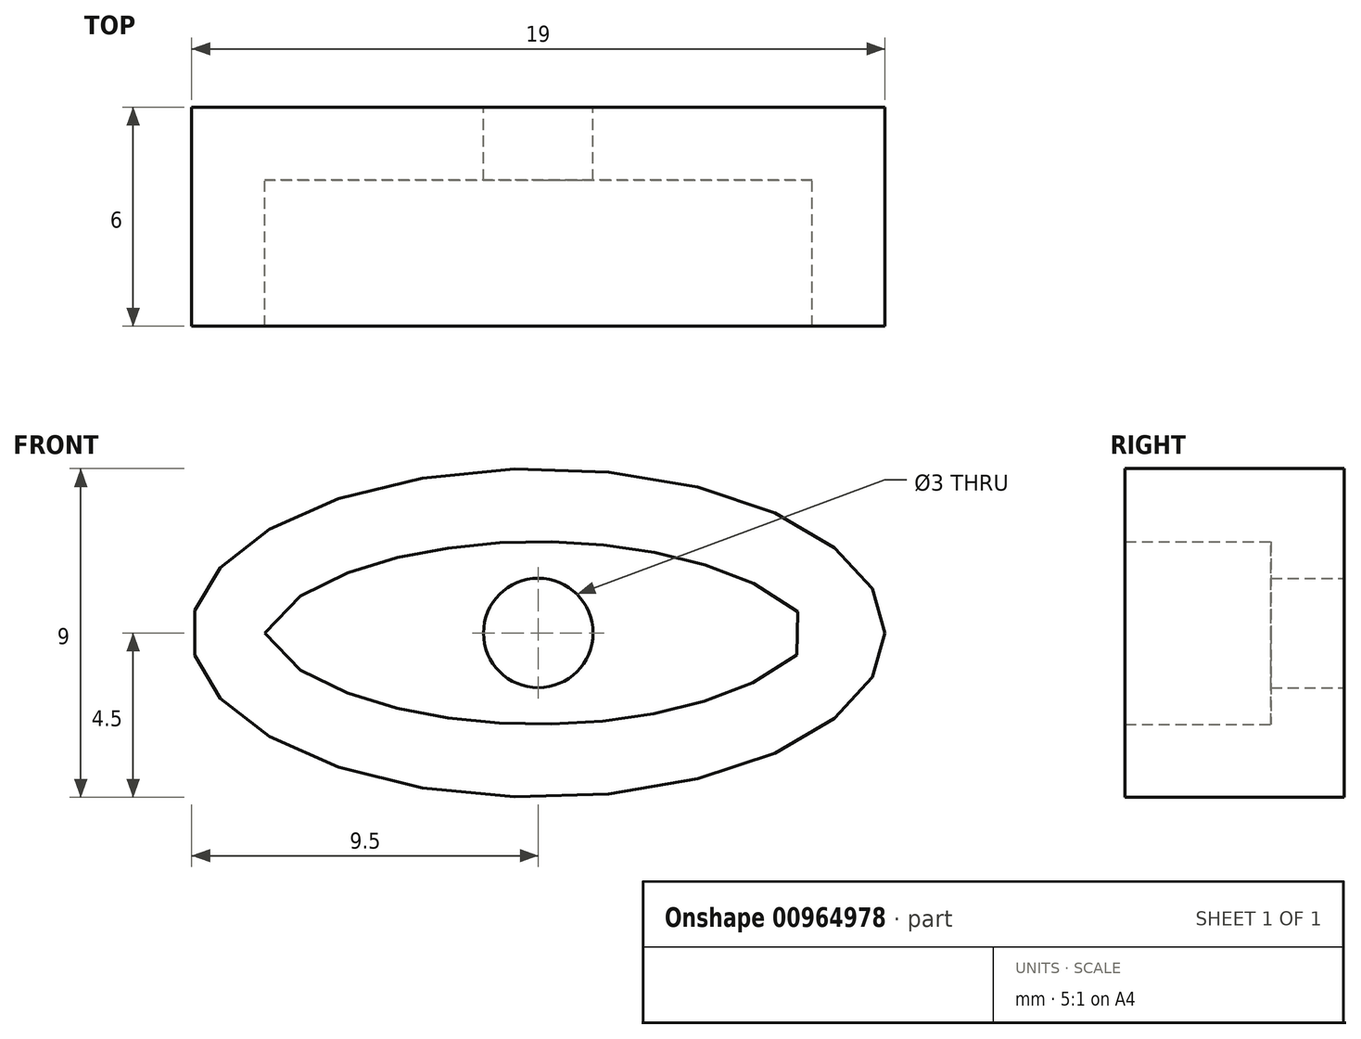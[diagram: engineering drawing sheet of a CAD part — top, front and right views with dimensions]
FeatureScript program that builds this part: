
annotation { "Feature Type Name" : "Feature", "Feature Type Description" : "" }
export const myFeature = defineFeature(function(context is Context, id is Id, definition is map)
    precondition{}
    {
        {
            var Q0;
            Q0=qCreatedBy(makeId("Front.planeOp"),FACE);
            var sketch = newSketch(context, id + "F0", { "sketchPlane" : qUnion([Q0])});
            skEllipse(sketch, "E0", {"center": v(0, 0) * mm, "majorRadius": 9.5 * mm, "minorRadius": 4.5 * mm, "majorAxis": v(1, 0)});
            skSolve(sketch);
        }
        {
            var Q0;
            Q0=makeQuery(id+"F0.imprint","IMPRINT",FACE,{"disambiguationData":[TD([[makeQuery(id+"F0.imprint","IMPRINT",EDGE,{"derivedFrom":sQuery(id+"F0.wireOp",EDGE,"E0")}),1.0]])]});
            var Q1;
            Q1=sQuery(id+"F0.wireOp",EDGE,"E0");
            extrude(context, id + "F1", {"entities" : qUnion([Q0]), "surfaceEntities" : qUnion([Q1]), "endBound" : BoundingType.SYMMETRIC, "depth" : 6 * mm, "offsetDistance" : 25 * mm});
        }
        {
            var Q0;
            Q0=makeQuery(id+"F1.opExtrude","CAP_FACE",FACE,{"disambiguationData":[OSD([sQuery(id+"F0.wireOp",EDGE,"E0")])],"isStart":false});
            shell(context, id + "F2", {"entities" : qUnion([Q0]), "thickness" : 2 * mm});
        }
        {
            var Q0;
            Q0=makeQuery(id+"F1.opExtrude","CAP_FACE",FACE,{"disambiguationData":[OSD([sQuery(id+"F0.wireOp",EDGE,"E0")])],"isStart":true});
            var sketch = newSketch(context, id + "F3", { "sketchPlane" : qUnion([Q0])});
            skEllipse(sketch, "E1.0", {"center": v(0, 0) * mm, "majorRadius": 12.5 * mm, "minorRadius": 6 * mm, "majorAxis": v(-1, 0)});
            skCircle(sketch, "E2", {"center": v(0, 0) * mm, "radius": 1.5 * mm});
            skSolve(sketch);
        }
        {
            var Q0;
            Q0=makeQuery(id+"F3.imprint","IMPRINT",FACE,{"disambiguationData":[TD([[makeQuery(id+"F3.imprint","IMPRINT",EDGE,{"derivedFrom":sQuery(id+"F3.wireOp",EDGE,"E2")}),1.0]])]});
            extrude(context, id + "F4", {"entities" : qUnion([Q0]), "operationType" : NewBodyOperationType.REMOVE, "endBound" : BoundingType.THROUGH_ALL, "oppositeDirection" : true, "depth" : 25 * mm, "offsetDistance" : 25 * mm, "hasSecondDirection" : true, "secondDirectionBound" : SecondDirectionBoundingType.THROUGH_ALL, "secondDirectionOppositeDirection" : false, "secondDirectionDepth" : 25 * mm});
        }
    });
